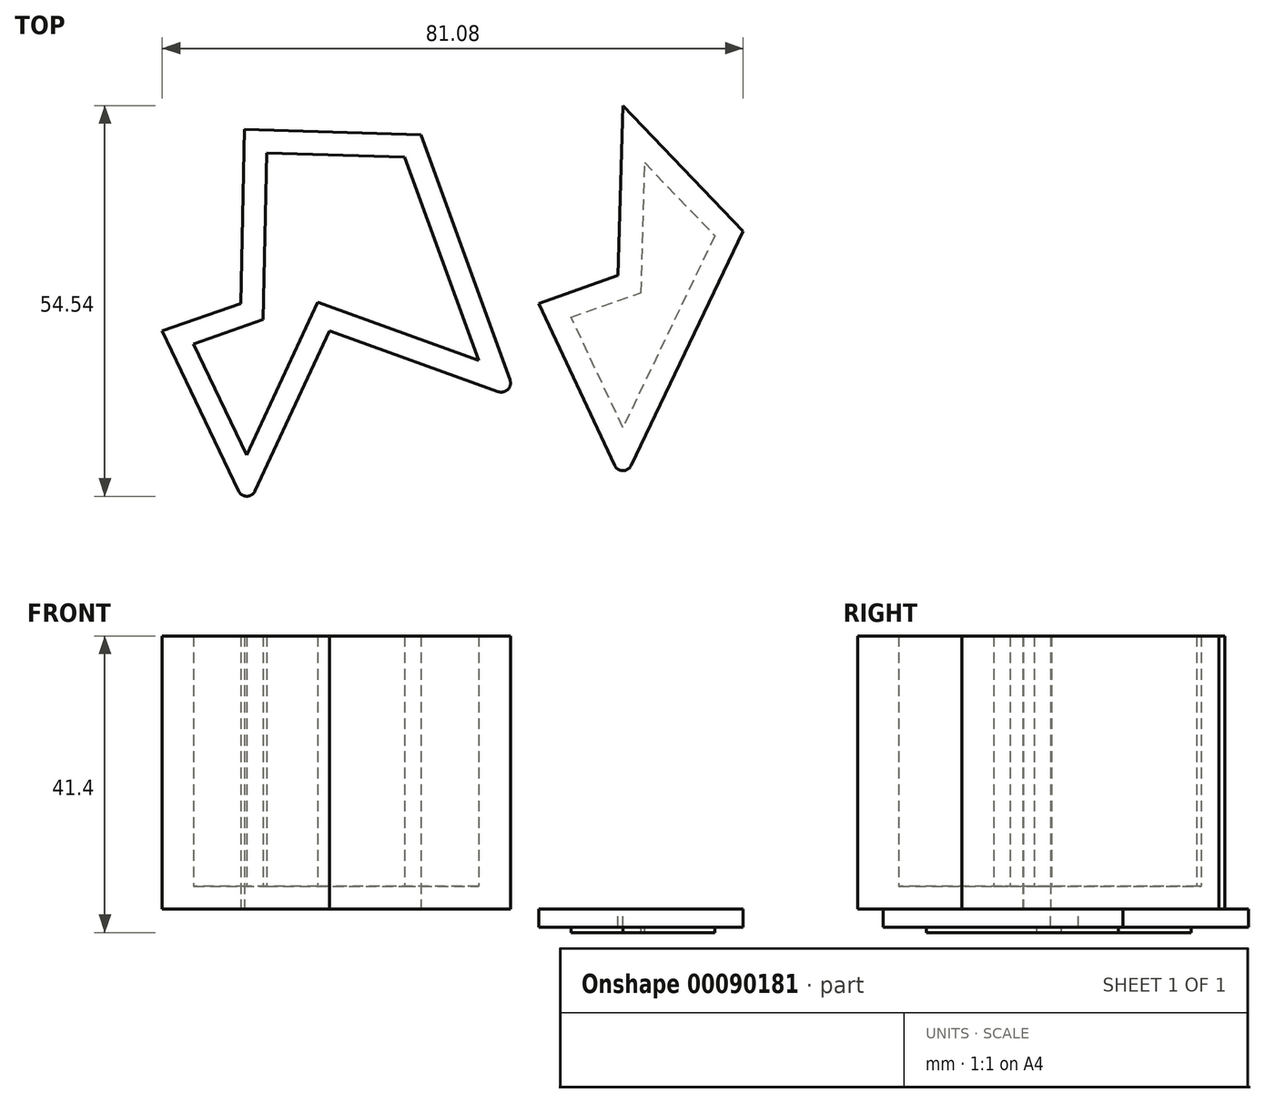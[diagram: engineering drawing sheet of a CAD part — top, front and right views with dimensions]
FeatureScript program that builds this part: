
annotation { "Feature Type Name" : "Feature", "Feature Type Description" : "" }
export const myFeature = defineFeature(function(context is Context, id is Id, definition is map)
    precondition{}
    {
        {
            var Q0;
            Q0=qCreatedBy(makeId("Top.planeOp"),FACE);
            var sketch = newSketch(context, id + "F0", { "sketchPlane" : qUnion([Q0])});
            skLineSegment(sketch, "E0", {"start": v(-21.03, 17.76) * mm, "end": v(3.55, 16.97) * mm});
            skLineSegment(sketch, "E1", {"start": v(3.55, 16.97) * mm, "end": v(16.93, -19.77) * mm});
            skLineSegment(sketch, "E2", {"start": v(16.93, -19.77) * mm, "end": v(-9.17, -10.37) * mm});
            skLineSegment(sketch, "E3", {"start": v(-9.17, -10.37) * mm, "end": v(-20.7, -35.17) * mm});
            skLineSegment(sketch, "E4", {"start": v(-20.7, -35.17) * mm, "end": v(-32.53, -10.4) * mm});
            skLineSegment(sketch, "E5", {"start": v(-32.53, -10.4) * mm, "end": v(-21.6, -6.54) * mm});
            skLineSegment(sketch, "E6", {"start": v(-21.6, -6.54) * mm, "end": v(-21.03, 17.76) * mm});
            skLineSegment(sketch, "E7", {"start": v(31.75, 21.08) * mm, "end": v(48.55, 3.52) * mm});
            skLineSegment(sketch, "E8", {"start": v(48.55, 3.52) * mm, "end": v(31.75, -31.58) * mm});
            skLineSegment(sketch, "E9", {"start": v(31.75, -31.58) * mm, "end": v(20, -6.57) * mm});
            skLineSegment(sketch, "E10", {"start": v(20, -6.57) * mm, "end": v(31.07, -2.65) * mm});
            skLineSegment(sketch, "E11", {"start": v(31.07, -2.65) * mm, "end": v(31.75, 21.08) * mm});
            skLineSegment(sketch, "E12.0", {"start": v(44.59, 2.9) * mm, "end": v(31.78, -23.88) * mm});
            skLineSegment(sketch, "E12.1", {"start": v(34.82, 13.1) * mm, "end": v(44.59, 2.9) * mm});
            skLineSegment(sketch, "E12.2", {"start": v(31.78, -23.88) * mm, "end": v(24.53, -8.47) * mm});
            skLineSegment(sketch, "E12.3", {"start": v(24.53, -8.47) * mm, "end": v(34.3, -5) * mm});
            skLineSegment(sketch, "E12.4", {"start": v(34.3, -5) * mm, "end": v(34.82, 13.1) * mm});
            skSolve(sketch);
        }
        {
            var Q0;
            Q0=makeQuery(id+"F0.imprint","IMPRINT",FACE,{"disambiguationData":[TD([[makeQuery(id+"F0.imprint","IMPRINT",EDGE,{"derivedFrom":sQuery(id+"F0.wireOp",EDGE,"E12.0")}),-1.0]])]});
            extrude(context, id + "F1", {"entities" : qUnion([Q0]), "oppositeDirection" : true, "depth" : 3.3 * mm});
        }
        {
            var Q0;
            Q0=makeQuery(id+"F0.imprint","IMPRINT",FACE,{"disambiguationData":[TD([[makeQuery(id+"F0.imprint","IMPRINT",EDGE,{"derivedFrom":sQuery(id+"F0.wireOp",EDGE,"E7")}),-1.0]])]});
            extrude(context, id + "F2", {"entities" : qUnion([Q0]), "operationType" : NewBodyOperationType.ADD, "oppositeDirection" : true, "depth" : 2.54 * mm});
        }
        {
            var Q0;
            Q0=makeQuery(id+"F0.imprint","IMPRINT",FACE,{"disambiguationData":[TD([[makeQuery(id+"F0.imprint","IMPRINT",EDGE,{"derivedFrom":sQuery(id+"F0.wireOp",EDGE,"E0")}),-1.0]])]});
            extrude(context, id + "F3", {"entities" : qUnion([Q0]), "depth" : 38.1 * mm});
        }
        {
            var Q0;
            Q0=makeQuery(id+"F3.opExtrude","CAP_FACE",FACE,{"disambiguationData":[OSD([sQuery(id+"F0.wireOp",EDGE,"E0"),sQuery(id+"F0.wireOp",EDGE,"E1"),sQuery(id+"F0.wireOp",EDGE,"E2"),sQuery(id+"F0.wireOp",EDGE,"E3"),sQuery(id+"F0.wireOp",EDGE,"E4"),sQuery(id+"F0.wireOp",EDGE,"E5"),sQuery(id+"F0.wireOp",EDGE,"E6")])],"isStart":false});
            shell(context, id + "F4", {"entities" : qUnion([Q0]), "thickness" : 3.17 * mm});
        }
        {
            var Q0;
            Q0=makeQuery(id+"F3.opExtrude","SWEPT_EDGE",EDGE,{"disambiguationData":[OSD([sQuery(id+"F0.wireOp",EDGE,"E3"),sQuery(id+"F0.wireOp",EDGE,"E4")])]});
            var Q1;
            Q1=makeQuery(id+"F3.opExtrude","SWEPT_EDGE",EDGE,{"disambiguationData":[OSD([sQuery(id+"F0.wireOp",EDGE,"E1"),sQuery(id+"F0.wireOp",EDGE,"E2")])]});
            var Q2;
            Q2=makeQuery(id+"F2.opExtrude","SWEPT_EDGE",EDGE,{"disambiguationData":[OSD([sQuery(id+"F0.wireOp",EDGE,"E8"),sQuery(id+"F0.wireOp",EDGE,"E9")])]});
            fillet(context, id + "F5", {"entities" : qUnion([Q0, Q1, Q2]), "radius" : 1.27 * mm, "tangentPropagation" : true, "allowEdgeOverflow" : false});
        }
    });
